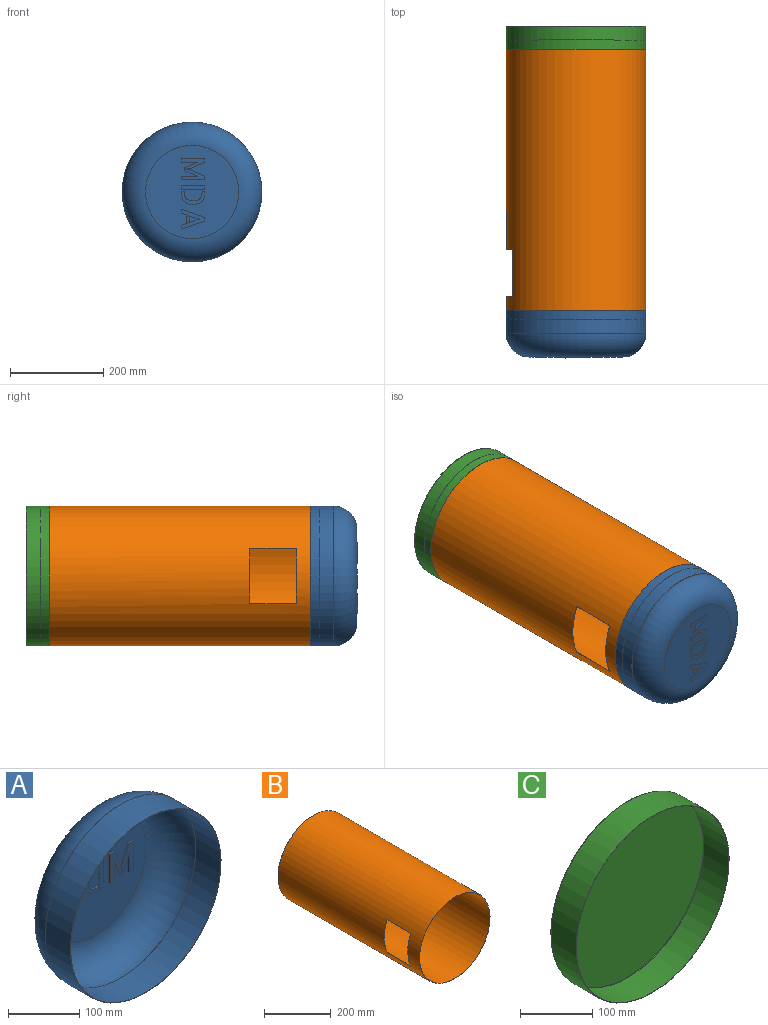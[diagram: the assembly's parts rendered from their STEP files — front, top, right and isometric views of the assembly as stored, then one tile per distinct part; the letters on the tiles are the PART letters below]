
ASSEMBLY  parts=3 mates=4
PART A: 125 faces, bbox 324.7x102x324.7 mm
  f0: cylinder r=150mm len=300mm, axis (0,1,0), area 47123.9mm2, adj f1,f3
  f1: plane 300x300mm, normal (0,-1,0), area 470.5mm2, adj f0,f4
  f2: plane 200x200mm, normal (0,1,0), area 28334.9mm2, adj f3,f16,f17,f18,f19,f20,f21,f22
  f3: torus R=100mm, axis (0,-1,0), area 65056mm2, adj f0,f2
  f4: cylinder r=149.5mm len=299mm, axis (0,1,0), area 46966.8mm2, adj f1,f6
  f5: plane 200x200mm, normal (0,-1,0), area 28334.9mm2, adj f6,f8,f9,f10,f11,f12,f13,f14
  f6: torus R=100mm, axis (0,-1,0), area 64249.9mm2, adj f4,f5
  f7: plane 49.98x21.7mm, normal (0,-1,0), area 632.8mm2, adj f8,f9,f10,f11,f12,f13,f14,f15
  f8: plane 30.85x13.42mm, normal (-0.92,0,0.4), area 100.9mm2, adj f5,f7,f9,f15
  f9: plane 12.55x3mm, normal (-1,0,0), area 37.7mm2, adj f5,f7,f8,f10
  f10: plane 3x2.17mm, normal (0,0,-1), area 6.5mm2, adj f5,f7,f9,f11
  f11: plane 27.81x11.25mm, normal (0.93,0,-0.38), area 90mm2, adj f5,f7,f10,f12
  f12: plane 34.39x3mm, normal (-1,0,0), area 103.2mm2, adj f5,f7,f11,f13
  f13: plane 8.28x3mm, normal (0,0,-1), area 24.8mm2, adj f5,f7,f12,f14
  f14: plane 49.98x3mm, normal (1,0,0), area 149.9mm2, adj f5,f7,f13,f15
  f15: plane 8.28x3mm, normal (0,0,1), area 24.8mm2, adj f5,f7,f8,f14
  f16: plane 8.28x2mm, normal (0,0,1), area 16.6mm2, adj f2,f17,f23,f24
  f17: plane 49.98x2mm, normal (1,0,0), area 100mm2, adj f2,f16,f18,f24
  f18: plane 8.28x2mm, normal (0,0,-1), area 16.6mm2, adj f2,f17,f19,f24
  f19: plane 34.39x2mm, normal (-1,0,0), area 68.8mm2, adj f2,f18,f20,f24
  f20: plane 27.81x11.25mm, normal (0.93,0,-0.38), area 60mm2, adj f2,f19,f21,f24
  f21: plane 2.17x2mm, normal (0,0,-1), area 4.3mm2, adj f2,f20,f22,f24
  f22: plane 12.55x2mm, normal (-1,0,0), area 25.1mm2, adj f2,f21,f23,f24
  f23: plane 30.85x13.42mm, normal (-0.92,0,0.4), area 67.3mm2, adj f2,f16,f22,f24
  f24: plane 49.98x21.7mm, normal (0,1,0), area 632.8mm2, adj f16,f17,f18,f19,f20,f21,f22,f23
  f25: plane 49.98x21.7mm, normal (0,-1,0), area 632.6mm2, adj f26,f27,f28,f29,f30,f31,f32,f33
  f26: plane 49.98x3mm, normal (-1,0,0), area 149.9mm2, adj f5,f25,f27,f33
  f27: plane 8.27x3mm, normal (0,0,-1), area 24.8mm2, adj f5,f25,f26,f28
  f28: plane 34.39x3mm, normal (1,0,0), area 103.2mm2, adj f5,f25,f27,f29
  f29: plane 27.81x11.19mm, normal (-0.93,0,-0.37), area 89.9mm2, adj f5,f25,f28,f30
  f30: plane 3x2.25mm, normal (0,0,-1), area 6.7mm2, adj f5,f25,f29,f31
  f31: plane 12.41x3mm, normal (1,0,0), area 37.2mm2, adj f5,f25,f30,f32
  f32: plane 30.99x13.43mm, normal (0.92,0,0.4), area 101.3mm2, adj f5,f25,f31,f33
  f33: plane 8.27x3mm, normal (0,0,1), area 24.8mm2, adj f5,f25,f26,f32
  f34: plane 8.27x2mm, normal (0,0,1), area 16.5mm2, adj f2,f35,f41,f42
  f35: plane 30.99x13.43mm, normal (0.92,0,0.4), area 67.6mm2, adj f2,f34,f36,f42
  f36: plane 12.41x2mm, normal (1,0,0), area 24.8mm2, adj f2,f35,f37,f42
  f37: plane 2.25x2mm, normal (0,0,-1), area 4.5mm2, adj f2,f36,f38,f42
  f38: plane 27.81x11.19mm, normal (-0.93,0,-0.37), area 60mm2, adj f2,f37,f39,f42
  f39: plane 34.39x2mm, normal (1,0,0), area 68.8mm2, adj f2,f38,f40,f42
  f40: plane 8.27x2mm, normal (0,0,-1), area 16.5mm2, adj f2,f39,f41,f42
  f41: plane 49.98x2mm, normal (-1,0,0), area 100mm2, adj f2,f34,f40,f42
  f42: plane 49.98x21.7mm, normal (0,1,0), area 632.6mm2, adj f34,f35,f36,f37,f38,f39,f40,f41
  f43: plane 49.98x8.14mm, normal (0,-1,0), area 406.7mm2, adj f44,f45,f46,f47
  f44: plane 49.98x3mm, normal (-1,0,0), area 149.9mm2, adj f5,f43,f45,f47
  f45: plane 8.14x3mm, normal (0,0,-1), area 24.4mm2, adj f5,f43,f44,f46
  f46: plane 49.98x3mm, normal (1,0,0), area 149.9mm2, adj f5,f43,f45,f47
  f47: plane 8.14x3mm, normal (0,0,1), area 24.4mm2, adj f5,f43,f44,f46
  f48: plane 8.14x2mm, normal (0,0,1), area 16.3mm2, adj f2,f49,f51,f52
  f49: plane 49.98x2mm, normal (1,0,0), area 100mm2, adj f2,f48,f50,f52
  f50: plane 8.14x2mm, normal (0,0,-1), area 16.3mm2, adj f2,f49,f51,f52
  f51: plane 49.98x2mm, normal (-1,0,0), area 100mm2, adj f2,f48,f50,f52
  f52: plane 49.98x8.14mm, normal (0,1,0), area 406.7mm2, adj f48,f49,f50,f51
  f53: plane 49.98x29.44mm, normal (0,-1,0), area 563mm2, adj f54,f55,f56,f57,f58,f59,f60,f61
  f54: extruded ~7.93x5.32mm, area 28.9mm2, adj f5,f53,f55,f75
  f55: extruded ~7.56x4.71mm, area 26.9mm2, adj f5,f53,f54,f56
  f56: extruded ~8.72x3mm, area 26.7mm2, adj f5,f53,f55,f57
  f57: extruded ~10.54x3mm, area 32mm2, adj f5,f53,f56,f58
  f58: extruded ~7.32x3.36mm, area 24.3mm2, adj f5,f53,f57,f59
  f59: extruded ~4.64x4.58mm, area 19.7mm2, adj f5,f53,f58,f60
  f60: extruded ~4.92x3mm, area 16.6mm2, adj f5,f53,f59,f61
  f61: extruded ~4.34x3mm, area 13.4mm2, adj f5,f53,f60,f62
  f62: extruded ~3x2.91mm, area 8.8mm2, adj f5,f53,f61,f63
  f63: plane 8.01x3mm, normal (0,0,-1), area 24mm2, adj f5,f53,f62,f64
  f64: plane 5.97x3mm, normal (1,0,0), area 17.9mm2, adj f5,f53,f63,f65
  f65: plane 5.3x3mm, normal (0,0,1), area 15.9mm2, adj f5,f53,f64,f66
  f66: extruded ~11.93x5.29mm, area 40.8mm2, adj f5,f53,f65,f67
  f67: extruded ~15.33x3.66mm, area 48mm2, adj f5,f53,f66,f68
  f68: extruded ~6.17x3mm, area 18.7mm2, adj f5,f53,f67,f69
  f69: extruded ~5.52x3mm, area 18.9mm2, adj f5,f53,f68,f70
  f70: extruded ~5.8x4mm, area 21.3mm2, adj f5,f53,f69,f71
  f71: extruded ~9.49x3mm, area 29mm2, adj f5,f53,f70,f72
  f72: plane 3x1.98mm, normal (0,0,-1), area 5.9mm2, adj f5,f53,f71,f73
  f73: plane 6.16x3mm, normal (1,0,0), area 18.5mm2, adj f5,f53,f72,f74
  f74: plane 4.15x3mm, normal (0,0,1), area 12.4mm2, adj f5,f53,f73,f75
  f75: extruded ~11.08x3mm, area 34mm2, adj f5,f53,f54,f74
  f76: extruded ~11.08x2mm, area 22.7mm2, adj f2,f77,f97,f98
  f77: plane 4.15x2mm, normal (0,0,1), area 8.3mm2, adj f2,f76,f78,f98
  f78: plane 6.16x2mm, normal (1,0,0), area 12.3mm2, adj f2,f77,f79,f98
  f79: plane 2x1.98mm, normal (0,0,-1), area 3.9mm2, adj f2,f78,f80,f98
  f80: extruded ~9.49x2mm, area 19.3mm2, adj f2,f79,f81,f98
  f81: extruded ~5.8x4mm, area 14.2mm2, adj f2,f80,f82,f98
  f82: extruded ~5.52x2.88mm, area 12.6mm2, adj f2,f81,f83,f98
  f83: extruded ~6.17x2mm, area 12.5mm2, adj f2,f82,f84,f98
  f84: extruded ~15.33x3.66mm, area 32mm2, adj f2,f83,f85,f98
  f85: extruded ~11.93x5.29mm, area 27.2mm2, adj f2,f84,f86,f98
  f86: plane 5.3x2mm, normal (0,0,1), area 10.6mm2, adj f2,f85,f87,f98
  f87: plane 5.97x2mm, normal (1,0,0), area 11.9mm2, adj f2,f86,f88,f98
  f88: plane 8.01x2mm, normal (0,0,-1), area 16mm2, adj f2,f87,f89,f98
  f89: extruded ~2.91x2mm, area 5.8mm2, adj f2,f88,f90,f98
  f90: extruded ~4.34x2mm, area 9mm2, adj f2,f89,f91,f98
  f91: extruded ~4.92x2.54mm, area 11.1mm2, adj f2,f90,f92,f98
  f92: extruded ~4.64x4.58mm, area 13.1mm2, adj f2,f91,f93,f98
  f93: extruded ~7.32x3.36mm, area 16.2mm2, adj f2,f92,f94,f98
  f94: extruded ~10.54x2mm, area 21.3mm2, adj f2,f93,f95,f98
  f95: extruded ~8.72x2mm, area 17.8mm2, adj f2,f94,f96,f98
  f96: extruded ~7.56x4.71mm, area 17.9mm2, adj f2,f95,f97,f98
  f97: extruded ~7.93x5.32mm, area 19.2mm2, adj f2,f76,f96,f98
  f98: plane 49.98x29.44mm, normal (0,1,0), area 563mm2, adj f76,f77,f78,f79,f80,f81,f82,f83
  f99: plane 49.91x42.93mm, normal (0,-1,0), area 785.3mm2, adj f100,f101,f102,f103,f104,f105,f106
  f100: plane 37.44x12.96mm, normal (0.95,0,-0.33), area 118.8mm2, adj f5,f99,f101,f106
  f101: plane 37.44x13.09mm, normal (-0.94,0,-0.33), area 119mm2, adj f5,f99,f100,f102
  f102: plane 8.47x3mm, normal (0,0,-1), area 25.4mm2, adj f5,f99,f101,f103
  f103: plane 49.91x17.49mm, normal (0.94,0,0.33), area 158.7mm2, adj f5,f99,f102,f104
  f104: plane 8.07x3mm, normal (0,0,1), area 24.2mm2, adj f5,f99,f103,f105
  f105: plane 49.91x17.36mm, normal (-0.94,0,0.33), area 158.5mm2, adj f5,f99,f104,f106
  f106: plane 8.41x3mm, normal (0,0,-1), area 25.2mm2, adj f5,f99,f100,f105
  f107: plane 8.41x2mm, normal (0,0,-1), area 16.8mm2, adj f2,f108,f113,f114
  f108: plane 49.91x17.36mm, normal (-0.94,0,0.33), area 105.7mm2, adj f2,f107,f109,f114
  f109: plane 8.07x2mm, normal (0,0,1), area 16.1mm2, adj f2,f108,f110,f114
  f110: plane 49.91x17.49mm, normal (0.94,0,0.33), area 105.8mm2, adj f2,f109,f111,f114
  f111: plane 8.47x2mm, normal (0,0,-1), area 16.9mm2, adj f2,f110,f112,f114
  f112: plane 37.44x13.09mm, normal (-0.94,0,-0.33), area 79.3mm2, adj f2,f111,f113,f114
  f113: plane 37.44x12.96mm, normal (0.95,0,-0.33), area 79.2mm2, adj f2,f107,f112,f114
  f114: plane 49.91x42.93mm, normal (0,1,0), area 785.3mm2, adj f107,f108,f109,f110,f111,f112,f113
  f115: plane 12.96x5.5mm, normal (0,-1,0), area 60.6mm2, adj f116,f117,f118,f119
  f116: plane 12.96x3mm, normal (0,0,-1), area 38.9mm2, adj f5,f115,f117,f119
  f117: plane 5.5x3mm, normal (0.95,0,0.33), area 17.5mm2, adj f5,f115,f116,f118
  f118: plane 9.09x3mm, normal (0,0,1), area 27.3mm2, adj f5,f115,f117,f119
  f119: plane 5.5x3mm, normal (-0.94,0,0.34), area 17.5mm2, adj f5,f115,f116,f118
  f120: plane 5.5x2mm, normal (-0.94,0,0.34), area 11.7mm2, adj f2,f121,f123,f124
  f121: plane 9.09x2mm, normal (0,0,1), area 18.2mm2, adj f2,f120,f122,f124
  f122: plane 5.5x2mm, normal (0.95,0,0.33), area 11.6mm2, adj f2,f121,f123,f124
  f123: plane 12.96x2mm, normal (0,0,-1), area 25.9mm2, adj f2,f120,f122,f124
  f124: plane 12.96x5.5mm, normal (0,1,0), area 60.6mm2, adj f120,f121,f122,f123
PART B: 8 faces, bbox 299x600x299 mm
  f0: cylinder r=149.5mm len=600mm, axis (0,1,0), area 551253.7mm2, adj f1,f2,f4,f5,f6,f7
  f1: plane 299x299mm, normal (0,-1,0), area 468.9mm2, adj f0,f3
  f2: plane 299x299mm, normal (0,1,0), area 468.9mm2, adj f0,f3
  f3: cylinder r=149mm len=600mm, axis (0,1,0), area 549366.2mm2, adj f1,f2,f4,f5,f6,f7
  f4: plane 100x0.55mm, normal (0,0,-1), area 54.6mm2, adj f0,f3,f6,f7
  f5: plane 100x0.55mm, normal (0,0,1), area 54.6mm2, adj f0,f3,f6,f7
  f6: plane 120x13.11mm, normal (0,1,0), area 61.7mm2, adj f0,f3,f4,f5
  f7: plane 120x13.11mm, normal (0,-1,0), area 61.7mm2, adj f0,f3,f4,f5
PART C: 7 faces, bbox 324.7x50x324.7 mm
  f0: cylinder r=150mm len=300mm, axis (0,1,0), area 46181.4mm2, adj f1,f6
  f1: plane 300x300mm, normal (0,-1,0), area 470.5mm2, adj f0,f3
  f2: plane 298x298mm, normal (0,1,0), area 69746.5mm2, adj f6
  f3: cylinder r=149.5mm len=299mm, axis (0,1,0), area 46027.5mm2, adj f1,f5
  f4: plane 298x298mm, normal (0,-1,0), area 69746.5mm2, adj f5
  f5: torus R=149mm, axis (0,-1,0), area 736.9mm2, adj f3,f4
  f6: torus R=149mm, axis (0,-1,0), area 1476.9mm2, adj f0,f2
PLACE A rot(axis=(0.71,0,0.71),180deg) t=(-292.55,-676.51,-161.53)mm
PLACE B t=(-292.55,3.49,-161.53)mm fixed
PLACE C rot(axis=(0,1,0),90deg) t=(-292.55,33.49,-161.53)mm
MATE cylindrical C.f0 <-> B.f0  axis (0,-1,0) through (-292.55,-16.51,-161.53)mm
MATE fastened C.f0 <-> B.f0  axis (0,-1,0) through (-292.55,-16.51,-161.53)mm
MATE fastened A.f0 <-> B.f0  axis (0,1,0) through (-292.55,-576.51,-161.53)mm
MATE cylindrical A.f0 <-> B.f0  axis (0,1,0) through (-292.55,-576.51,-161.53)mm
